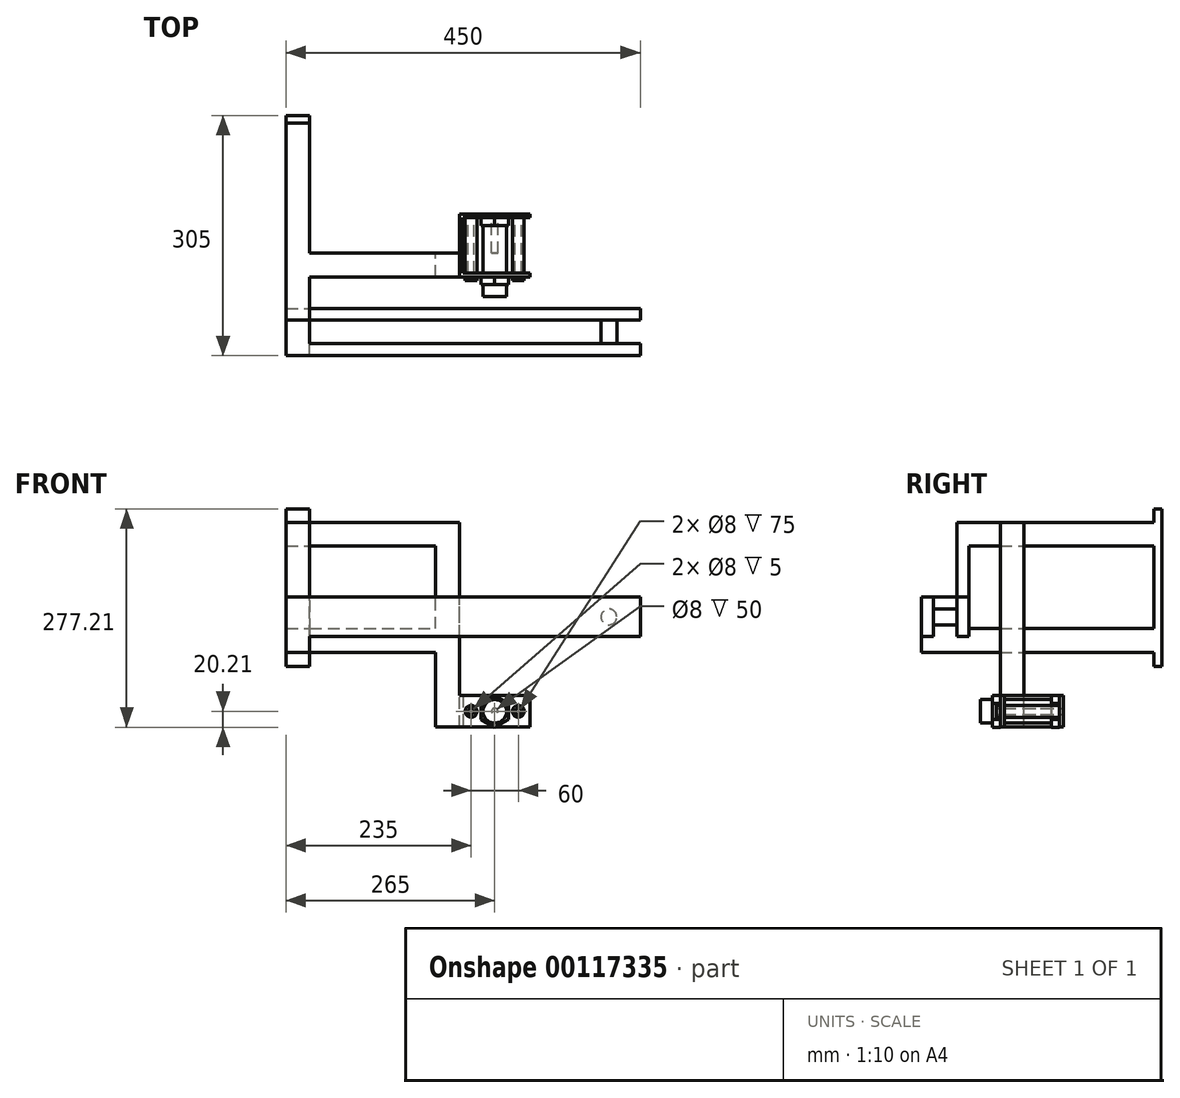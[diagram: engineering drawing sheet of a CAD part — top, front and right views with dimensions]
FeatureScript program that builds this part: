
annotation { "Feature Type Name" : "Feature", "Feature Type Description" : "" }
export const myFeature = defineFeature(function(context is Context, id is Id, definition is map)
    precondition{}
    {
        {
            var Q0;
            Q0=qCreatedBy(makeId("Front.planeOp"),FACE);
            var sketch = newSketch(context, id + "F0", { "sketchPlane" : qUnion([Q0])});
            skLineSegment(sketch, "E0.bottom", {"start": v(45, -20) * mm, "end": v(-45, -20) * mm});
            skLineSegment(sketch, "E0.top", {"start": v(45, 20) * mm, "end": v(-45, 20) * mm});
            skLineSegment(sketch, "E0.left", {"start": v(45, -20) * mm, "end": v(45, 20) * mm});
            skLineSegment(sketch, "E0.right", {"start": v(-45, -20) * mm, "end": v(-45, 20) * mm});
            skPoint(sketch, "E0.middle", {"position": v(0, 0) * mm});
            skCircle(sketch, "E1", {"center": v(0, 0) * mm, "radius": 4 * mm});
            skCircle(sketch, "E2", {"center": v(30, 0) * mm, "radius": 4 * mm});
            skCircle(sketch, "E3", {"center": v(-30, 0) * mm, "radius": 4 * mm});
            skSolve(sketch);
        }
        {
            var Q0;
            Q0 = qSketchRegion(id + "F0", true);
            extrude(context, id + "F1", {"entities" : qUnion([Q0]), "depth" : 5 * mm});
        }
        {
            var Q0;
            Q0=makeQuery(id+"F1.opExtrude","CAP_FACE",FACE,{"disambiguationData":[OSD([sQuery(id+"F0.wireOp",EDGE,"E0.bottom"),sQuery(id+"F0.wireOp",EDGE,"E0.top"),sQuery(id+"F0.wireOp",EDGE,"E0.left"),sQuery(id+"F0.wireOp",EDGE,"E0.right"),sQuery(id+"F0.wireOp",EDGE,"E1"),sQuery(id+"F0.wireOp",EDGE,"E2"),sQuery(id+"F0.wireOp",EDGE,"E3")])],"isStart":false});
            var sketch = newSketch(context, id + "F2", { "sketchPlane" : qUnion([Q0])});
            skCircle(sketch, "E4.cCircle", {"center": v(0, 0) * mm, "radius": 17.5 * mm, "construction": true});
            skLineSegment(sketch, "E4.0", {"start": v(17.5, 10.1) * mm, "end": v(17.5, -10.1) * mm});
            skLineSegment(sketch, "E4.1", {"start": v(17.5, -10.1) * mm, "end": v(0, -20.2) * mm});
            skLineSegment(sketch, "E4.2", {"start": v(0, -20.2) * mm, "end": v(-17.5, -10.1) * mm});
            skLineSegment(sketch, "E4.3", {"start": v(-17.5, -10.1) * mm, "end": v(-17.5, 10.1) * mm});
            skLineSegment(sketch, "E4.4", {"start": v(-17.5, 10.1) * mm, "end": v(0, 20.2) * mm});
            skLineSegment(sketch, "E4.5", {"start": v(0, 20.2) * mm, "end": v(17.5, 10.1) * mm});
            skPoint(sketch, "E4.0.midPoint", {"position": v(17.5, 0) * mm});
            skSolve(sketch);
        }
        {
            var Q0;
            Q0 = qSketchRegion(id + "F2", true);
            extrude(context, id + "F3", {"entities" : qUnion([Q0]), "operationType" : NewBodyOperationType.ADD, "depth" : 10 * mm});
        }
        {
            var Q0;
            Q0=makeQuery(id+"F3.opExtrude","CAP_FACE",FACE,{"disambiguationData":[OSD([sQuery(id+"F2.wireOp",EDGE,"E4.0"),sQuery(id+"F2.wireOp",EDGE,"E4.1"),sQuery(id+"F2.wireOp",EDGE,"E4.2"),sQuery(id+"F2.wireOp",EDGE,"E4.3"),sQuery(id+"F2.wireOp",EDGE,"E4.4"),sQuery(id+"F2.wireOp",EDGE,"E4.5")])],"isStart":false});
            var sketch = newSketch(context, id + "F4", { "sketchPlane" : qUnion([Q0])});
            skCircle(sketch, "E5", {"center": v(0, 0) * mm, "radius": 15 * mm});
            skSolve(sketch);
        }
        {
            var Q0;
            Q0 = qSketchRegion(id + "F4", true);
            extrude(context, id + "F5", {"entities" : qUnion([Q0]), "operationType" : NewBodyOperationType.ADD, "depth" : 60 * mm});
        }
        {
            var Q0;
            {var subQ0=sQuery(id+"F0.wireOp",EDGE,"E2");var subQ2=sQuery(id+"F0.wireOp",EDGE,"E0.left");var subQ5=sQuery(id+"F0.wireOp",EDGE,"E0.top");var subQ6=sQuery(id+"F0.wireOp",EDGE,"E0.bottom");Q0=makeQuery(id+"F3.boolean.opBoolean","SPLIT",FACE,{"disambiguationData":[TD([makeQuery(id+"F1.opExtrude","SWEPT_FACE",FACE,{"disambiguationData":[OSD([subQ2])]})])],"derivedFrom":makeQuery(id+"F1.opExtrude","CAP_FACE",FACE,{"disambiguationData":[OSD([subQ6,subQ5,subQ2,sQuery(id+"F0.wireOp",EDGE,"E0.right"),sQuery(id+"F0.wireOp",EDGE,"E1"),subQ0,sQuery(id+"F0.wireOp",EDGE,"E3")])],"isStart":false})});}
            var sketch = newSketch(context, id + "F6", { "sketchPlane" : qUnion([Q0])});
            skCircle(sketch, "E6", {"center": v(30, 0) * mm, "radius": 7.5 * mm});
            skCircle(sketch, "E7", {"center": v(-30, 0) * mm, "radius": 7.5 * mm});
            skCircle(sketch, "E8", {"center": v(30, 0) * mm, "radius": 4 * mm});
            skCircle(sketch, "E9", {"center": v(-30, 0) * mm, "radius": 4 * mm});
            skSolve(sketch);
        }
        {
            var Q0;
            Q0 = qSketchRegion(id + "F6", true);
            extrude(context, id + "F7", {"entities" : qUnion([Q0]), "operationType" : NewBodyOperationType.ADD, "depth" : 80 * mm});
        }
        {
            var Q0;
            Q0=makeQuery(id+"F5.opExtrude","CAP_FACE",FACE,{"disambiguationData":[OSD([sQuery(id+"F4.wireOp",EDGE,"E5")])],"isStart":false});
            var sketch = newSketch(context, id + "F8", { "sketchPlane" : qUnion([Q0])});
            skLineSegment(sketch, "E10.bottom", {"start": v(45, -20) * mm, "end": v(-45, -20) * mm});
            skLineSegment(sketch, "E10.top", {"start": v(45, 20) * mm, "end": v(-45, 20) * mm});
            skLineSegment(sketch, "E10.left", {"start": v(45, -20) * mm, "end": v(45, 20) * mm});
            skLineSegment(sketch, "E10.right", {"start": v(-45, -20) * mm, "end": v(-45, 20) * mm});
            skPoint(sketch, "E10.middle", {"position": v(0, 0) * mm});
            skSolve(sketch);
        }
        {
            var Q0;
            Q0 = qSketchRegion(id + "F8", true);
            extrude(context, id + "F9", {"entities" : qUnion([Q0]), "operationType" : NewBodyOperationType.ADD, "depth" : 5 * mm});
        }
        {
            var Q0;
            Q0=makeQuery(id+"F9.opExtrude","CAP_FACE",FACE,{"disambiguationData":[OSD([sQuery(id+"F8.wireOp",EDGE,"E10.bottom"),sQuery(id+"F8.wireOp",EDGE,"E10.top"),sQuery(id+"F8.wireOp",EDGE,"E10.left"),sQuery(id+"F8.wireOp",EDGE,"E10.right")])],"isStart":false});
            var sketch = newSketch(context, id + "F10", { "sketchPlane" : qUnion([Q0])});
            skCircle(sketch, "E11.cCircle", {"center": v(0, 0) * mm, "radius": 17.5 * mm, "construction": true});
            skLineSegment(sketch, "E11.0", {"start": v(17.52, -10.07) * mm, "end": v(0.04, -20.2) * mm});
            skLineSegment(sketch, "E11.1", {"start": v(0.04, -20.2) * mm, "end": v(-17.48, -10.14) * mm});
            skLineSegment(sketch, "E11.2", {"start": v(-17.48, -10.14) * mm, "end": v(-17.52, 10.07) * mm});
            skLineSegment(sketch, "E11.3", {"start": v(-17.52, 10.07) * mm, "end": v(-0.04, 20.2) * mm});
            skLineSegment(sketch, "E11.4", {"start": v(-0.04, 20.2) * mm, "end": v(17.48, 10.14) * mm});
            skLineSegment(sketch, "E11.5", {"start": v(17.48, 10.14) * mm, "end": v(17.52, -10.07) * mm});
            skPoint(sketch, "E11.0.midPoint", {"position": v(8.78, -15.14) * mm});
            skSolve(sketch);
        }
        {
            var Q0;
            Q0 = qSketchRegion(id + "F10", true);
            extrude(context, id + "F11", {"entities" : qUnion([Q0]), "operationType" : NewBodyOperationType.ADD, "depth" : 10 * mm});
        }
        {
            var Q0;
            Q0=makeQuery(id+"F11.opExtrude","CAP_FACE",FACE,{"disambiguationData":[OSD([sQuery(id+"F10.wireOp",EDGE,"E11.0"),sQuery(id+"F10.wireOp",EDGE,"E11.1"),sQuery(id+"F10.wireOp",EDGE,"E11.2"),sQuery(id+"F10.wireOp",EDGE,"E11.3"),sQuery(id+"F10.wireOp",EDGE,"E11.4"),sQuery(id+"F10.wireOp",EDGE,"E11.5")])],"isStart":false});
            var sketch = newSketch(context, id + "F12", { "sketchPlane" : qUnion([Q0])});
            skCircle(sketch, "E12", {"center": v(0, 0) * mm, "radius": 15 * mm});
            skSolve(sketch);
        }
        {
            var Q0;
            Q0 = qSketchRegion(id + "F12", true);
            extrude(context, id + "F13", {"entities" : qUnion([Q0]), "operationType" : NewBodyOperationType.ADD, "depth" : 15 * mm});
        }
        {
            var Q0;
            {var subQ0=sQuery(id+"F0.wireOp",EDGE,"E0.right");var subQ1=sQuery(id+"F0.wireOp",EDGE,"E3");var subQ3=sQuery(id+"F0.wireOp",EDGE,"E0.top");var subQ4=sQuery(id+"F0.wireOp",EDGE,"E0.bottom");Q0=makeQuery(id+"F3.boolean.opBoolean","SPLIT",FACE,{"disambiguationData":[TD([makeQuery(id+"F1.opExtrude","SWEPT_FACE",FACE,{"disambiguationData":[OSD([subQ0])]})])],"derivedFrom":makeQuery(id+"F1.opExtrude","CAP_FACE",FACE,{"disambiguationData":[OSD([subQ4,subQ3,sQuery(id+"F0.wireOp",EDGE,"E0.left"),subQ0,sQuery(id+"F0.wireOp",EDGE,"E1"),sQuery(id+"F0.wireOp",EDGE,"E2"),subQ1])],"isStart":false})});}
            var sketch = newSketch(context, id + "F14", { "sketchPlane" : qUnion([Q0])});
            skLineSegment(sketch, "E13.bottom", {"start": v(-45, 20) * mm, "end": v(-40, 20) * mm});
            skLineSegment(sketch, "E13.top", {"start": v(-45, -20) * mm, "end": v(-40, -20) * mm});
            skLineSegment(sketch, "E13.left", {"start": v(-45, 20) * mm, "end": v(-45, -20) * mm});
            skLineSegment(sketch, "E13.right", {"start": v(-40, 20) * mm, "end": v(-40, -20) * mm});
            skSolve(sketch);
        }
        {
            var Q0;
            Q0 = qSketchRegion(id + "F14", true);
            var Q1;
            {var subQ0=sQuery(id+"F8.wireOp",EDGE,"E10.bottom");var subQ1=sQuery(id+"F8.wireOp",EDGE,"E10.right");var subQ2=sQuery(id+"F8.wireOp",EDGE,"E10.top");var subQ3=sQuery(id+"F8.wireOp",EDGE,"E10.left");Q1=makeQuery(id+"F9.boolean.opBoolean","SPLIT",FACE,{"disambiguationData":[TD([makeQuery(id+"F5.opExtrude","SWEPT_FACE",FACE,{"disambiguationData":[OSD([sQuery(id+"F4.wireOp",EDGE,"E5")])]})])],"derivedFrom":makeQuery(id+"F9.opExtrude","CAP_FACE",FACE,{"disambiguationData":[OSD([subQ0,subQ2,subQ3,subQ1])],"isStart":true})});}
            extrude(context, id + "F15", {"entities" : qUnion([Q0]), "operationType" : NewBodyOperationType.ADD, "endBound" : BoundingType.UP_TO_SURFACE, "endBoundEntityFace" : qUnion([Q1]), "depth" : 25 * mm});
        }
        {
            var Q0;
            Q0=makeQuery(id+"F1.opExtrude","CAP_FACE",FACE,{"disambiguationData":[OSD([sQuery(id+"F0.wireOp",EDGE,"E0.bottom"),sQuery(id+"F0.wireOp",EDGE,"E0.top"),sQuery(id+"F0.wireOp",EDGE,"E0.left"),sQuery(id+"F0.wireOp",EDGE,"E0.right"),sQuery(id+"F0.wireOp",EDGE,"E1"),sQuery(id+"F0.wireOp",EDGE,"E2"),sQuery(id+"F0.wireOp",EDGE,"E3")])],"isStart":true});
            var sketch = newSketch(context, id + "F16", { "sketchPlane" : qUnion([Q0])});
            skCircle(sketch, "E14", {"center": v(0, 0) * mm, "radius": 4 * mm});
            skSolve(sketch);
        }
        {
            var Q0;
            Q0 = qSketchRegion(id + "F16", true);
            extrude(context, id + "F17", {"entities" : qUnion([Q0]), "operationType" : NewBodyOperationType.REMOVE, "oppositeDirection" : true, "depth" : 50 * mm});
        }
        {
            var Q0;
            Q0=makeQuery(id+"F15.boolean.opBoolean","MERGE",FACE,{"derivedFrom":[makeQuery(id+"F1.opExtrude","SWEPT_FACE",FACE,{"disambiguationData":[OSD([sQuery(id+"F0.wireOp",EDGE,"E0.right")])]}),makeQuery(id+"F9.opExtrude","SWEPT_FACE",FACE,{"disambiguationData":[OSD([sQuery(id+"F8.wireOp",EDGE,"E10.right")])]}),makeQuery(id+"F15.opExtrude","SWEPT_FACE",FACE,{"disambiguationData":[OSD([sQuery(id+"F14.wireOp",EDGE,"E13.left")])]})]});
            var sketch = newSketch(context, id + "F18", { "sketchPlane" : qUnion([Q0])});
            skLineSegment(sketch, "E15.bottom", {"start": v(80, -20) * mm, "end": v(50, -20) * mm});
            skLineSegment(sketch, "E15.top", {"start": v(80, 240) * mm, "end": v(50, 240) * mm});
            skLineSegment(sketch, "E15.left", {"start": v(80, -20) * mm, "end": v(80, 240) * mm});
            skLineSegment(sketch, "E15.right", {"start": v(50, -20) * mm, "end": v(50, 240) * mm});
            skSolve(sketch);
        }
        {
            var Q0;
            Q0 = qSketchRegion(id + "F18", true);
            extrude(context, id + "F19", {"entities" : qUnion([Q0]), "operationType" : NewBodyOperationType.ADD, "depth" : 30 * mm});
        }
        {
            var Q0;
            Q0=makeQuery(id+"F19.opExtrude","CAP_FACE",FACE,{"disambiguationData":[OSD([sQuery(id+"F18.wireOp",EDGE,"E15.bottom"),sQuery(id+"F18.wireOp",EDGE,"E15.top"),sQuery(id+"F18.wireOp",EDGE,"E15.left"),sQuery(id+"F18.wireOp",EDGE,"E15.right")])],"isStart":false});
            var sketch = newSketch(context, id + "F20", { "sketchPlane" : qUnion([Q0])});
            skLineSegment(sketch, "E16.bottom", {"start": v(80, 75) * mm, "end": v(50, 75) * mm});
            skLineSegment(sketch, "E16.top", {"start": v(80, 105) * mm, "end": v(50, 105) * mm});
            skLineSegment(sketch, "E16.left", {"start": v(80, 75) * mm, "end": v(80, 105) * mm});
            skLineSegment(sketch, "E16.right", {"start": v(50, 75) * mm, "end": v(50, 105) * mm});
            skLineSegment(sketch, "E17.bottom", {"start": v(80, 240) * mm, "end": v(50, 240) * mm});
            skLineSegment(sketch, "E17.top", {"start": v(80, 210) * mm, "end": v(50, 210) * mm});
            skLineSegment(sketch, "E17.left", {"start": v(80, 240) * mm, "end": v(80, 210) * mm});
            skLineSegment(sketch, "E17.right", {"start": v(50, 240) * mm, "end": v(50, 210) * mm});
            skSolve(sketch);
        }
        {
            var Q0;
            Q0 = qSketchRegion(id + "F20", true);
            extrude(context, id + "F21", {"entities" : qUnion([Q0]), "operationType" : NewBodyOperationType.ADD, "depth" : 190 * mm});
        }
        {
            var Q0;
            {var subQ0=sQuery(id+"F8.wireOp",EDGE,"E10.right");var subQ2=sQuery(id+"F8.wireOp",EDGE,"E10.top");var subQ4=sQuery(id+"F8.wireOp",EDGE,"E10.bottom");var subQ6=makeQuery(id+"F7.opExtrude","SWEPT_FACE",FACE,{"disambiguationData":[OSD([sQuery(id+"F6.wireOp",EDGE,"E7")])]});var subQ10=sQuery(id+"F8.wireOp",EDGE,"E10.left");Q0=makeQuery(id+"F21.boolean.opBoolean","MERGE",FACE,{"derivedFrom":[makeQuery(id+"F19.boolean.opBoolean","MERGE",FACE,{"derivedFrom":[makeQuery(id+"F11.boolean.opBoolean","SPLIT",FACE,{"disambiguationData":[TD([subQ6])],"derivedFrom":makeQuery(id+"F9.boolean.opBoolean","SPLIT",FACE,{"disambiguationData":[TD([makeQuery(id+"F7.opExtrude","SWEPT_FACE",FACE,{"disambiguationData":[OSD([sQuery(id+"F6.wireOp",EDGE,"E6")])]})])],"derivedFrom":makeQuery(id+"F9.opExtrude","CAP_FACE",FACE,{"disambiguationData":[OSD([subQ4,subQ2,subQ10,subQ0])],"isStart":false})})}),makeQuery(id+"F19.opExtrude","SWEPT_FACE",FACE,{"disambiguationData":[OSD([sQuery(id+"F18.wireOp",EDGE,"E15.left")])]})]}),makeQuery(id+"F21.opExtrude","SWEPT_FACE",FACE,{"disambiguationData":[OSD([sQuery(id+"F20.wireOp",EDGE,"E16.left")])]}),makeQuery(id+"F21.opExtrude","SWEPT_FACE",FACE,{"disambiguationData":[OSD([sQuery(id+"F20.wireOp",EDGE,"E17.left")])]})]});}
            var sketch = newSketch(context, id + "F22", { "sketchPlane" : qUnion([Q0])});
            skLineSegment(sketch, "E18.bottom", {"start": v(-265, 75) * mm, "end": v(-235, 75) * mm});
            skLineSegment(sketch, "E18.top", {"start": v(-265, 105) * mm, "end": v(-235, 105) * mm});
            skLineSegment(sketch, "E18.left", {"start": v(-265, 75) * mm, "end": v(-265, 105) * mm});
            skLineSegment(sketch, "E18.right", {"start": v(-235, 75) * mm, "end": v(-235, 105) * mm});
            skLineSegment(sketch, "E19.bottom", {"start": v(-265, 210) * mm, "end": v(-235, 210) * mm});
            skLineSegment(sketch, "E19.top", {"start": v(-265, 240) * mm, "end": v(-235, 240) * mm});
            skLineSegment(sketch, "E19.left", {"start": v(-265, 210) * mm, "end": v(-265, 240) * mm});
            skLineSegment(sketch, "E19.right", {"start": v(-235, 210) * mm, "end": v(-235, 240) * mm});
            skSolve(sketch);
        }
        {
            var Q0;
            Q0 = qSketchRegion(id + "F22", true);
            extrude(context, id + "F23", {"entities" : qUnion([Q0]), "operationType" : NewBodyOperationType.ADD, "oppositeDirection" : true, "depth" : 205 * mm});
        }
        {
            var Q0;
            Q0 = qSketchRegion(id + "F22", true);
            extrude(context, id + "F24", {"entities" : qUnion([Q0]), "operationType" : NewBodyOperationType.ADD, "depth" : 40 * mm});
        }
        {
            var Q0;
            Q0=makeQuery(id+"F23.opExtrude","CAP_FACE",FACE,{"disambiguationData":[OSD([sQuery(id+"F22.wireOp",EDGE,"E18.bottom"),sQuery(id+"F22.wireOp",EDGE,"E18.top"),sQuery(id+"F22.wireOp",EDGE,"E18.left"),sQuery(id+"F22.wireOp",EDGE,"E18.right")])],"isStart":false});
            var sketch = newSketch(context, id + "F25", { "sketchPlane" : qUnion([Q0])});
            skLineSegment(sketch, "E20.bottom", {"start": v(265, 257) * mm, "end": v(235, 257) * mm});
            skLineSegment(sketch, "E20.top", {"start": v(265, 57) * mm, "end": v(235, 57) * mm});
            skLineSegment(sketch, "E20.left", {"start": v(265, 257) * mm, "end": v(265, 57) * mm});
            skLineSegment(sketch, "E20.right", {"start": v(235, 257) * mm, "end": v(235, 57) * mm});
            skSolve(sketch);
        }
        {
            var Q0;
            Q0 = qSketchRegion(id + "F25", true);
            extrude(context, id + "F26", {"entities" : qUnion([Q0]), "operationType" : NewBodyOperationType.ADD, "oppositeDirection" : true, "depth" : 10 * mm});
        }
        {
            var Q0;
            Q0=makeQuery(id+"F24.opExtrude","CAP_FACE",FACE,{"disambiguationData":[OSD([sQuery(id+"F22.wireOp",EDGE,"E18.bottom"),sQuery(id+"F22.wireOp",EDGE,"E18.top"),sQuery(id+"F22.wireOp",EDGE,"E18.left"),sQuery(id+"F22.wireOp",EDGE,"E18.right")])],"isStart":false});
            var sketch = newSketch(context, id + "F27", { "sketchPlane" : qUnion([Q0])});
            skLineSegment(sketch, "E21.bottom", {"start": v(-265, 75) * mm, "end": v(-235, 75) * mm});
            skLineSegment(sketch, "E21.top", {"start": v(-265, 240) * mm, "end": v(-235, 240) * mm});
            skLineSegment(sketch, "E21.left", {"start": v(-265, 75) * mm, "end": v(-265, 240) * mm});
            skLineSegment(sketch, "E21.right", {"start": v(-235, 75) * mm, "end": v(-235, 240) * mm});
            skSolve(sketch);
        }
        {
            var Q0;
            Q0 = qSketchRegion(id + "F27", true);
            extrude(context, id + "F28", {"entities" : qUnion([Q0]), "operationType" : NewBodyOperationType.ADD, "depth" : 60 * mm});
        }
        {
            var Q0;
            Q0=makeQuery(id+"F28.boolean.opBoolean","MERGE",FACE,{"derivedFrom":[makeQuery(id+"F24.opExtrude","SWEPT_FACE",FACE,{"disambiguationData":[OSD([sQuery(id+"F22.wireOp",EDGE,"E18.right")])]}),makeQuery(id+"F24.opExtrude","SWEPT_FACE",FACE,{"disambiguationData":[OSD([sQuery(id+"F22.wireOp",EDGE,"E19.right")])]}),makeQuery(id+"F28.opExtrude","SWEPT_FACE",FACE,{"disambiguationData":[OSD([sQuery(id+"F27.wireOp",EDGE,"E21.right")])]})]});
            var sketch = newSketch(context, id + "F29", { "sketchPlane" : qUnion([Q0])});
            skLineSegment(sketch, "E22.bottom", {"start": v(-180, 95) * mm, "end": v(-165, 95) * mm});
            skLineSegment(sketch, "E22.top", {"start": v(-180, 145) * mm, "end": v(-165, 145) * mm});
            skLineSegment(sketch, "E22.left", {"start": v(-180, 95) * mm, "end": v(-180, 145) * mm});
            skLineSegment(sketch, "E22.right", {"start": v(-120, 95) * mm, "end": v(-120, 145) * mm});
            skLineSegment(sketch, "E23", {"start": v(-165, 95) * mm, "end": v(-165, 145) * mm});
            skLineSegment(sketch, "E24", {"start": v(-135, 95) * mm, "end": v(-135, 145) * mm});
            skLineSegment(sketch, "E25.trimOffspring", {"start": v(-135, 145) * mm, "end": v(-120, 145) * mm});
            skLineSegment(sketch, "E26.trimOffspring", {"start": v(-135, 95) * mm, "end": v(-120, 95) * mm});
            skSolve(sketch);
        }
        {
            var Q0;
            Q0 = qSketchRegion(id + "F29", true);
            extrude(context, id + "F30", {"entities" : qUnion([Q0]), "operationType" : NewBodyOperationType.ADD, "depth" : 420 * mm});
        }
        {
            var Q0;
            Q0=makeQuery(id+"F28.boolean.opBoolean","MERGE",FACE,{"derivedFrom":[makeQuery(id+"F24.opExtrude","SWEPT_FACE",FACE,{"disambiguationData":[OSD([sQuery(id+"F22.wireOp",EDGE,"E18.right")])]}),makeQuery(id+"F24.opExtrude","SWEPT_FACE",FACE,{"disambiguationData":[OSD([sQuery(id+"F22.wireOp",EDGE,"E19.right")])]}),makeQuery(id+"F28.opExtrude","SWEPT_FACE",FACE,{"disambiguationData":[OSD([sQuery(id+"F27.wireOp",EDGE,"E21.right")])]})]});
            var sketch = newSketch(context, id + "F31", { "sketchPlane" : qUnion([Q0])});
            skLineSegment(sketch, "E27.bottom", {"start": v(-180, 145) * mm, "end": v(-135, 145) * mm});
            skLineSegment(sketch, "E27.top", {"start": v(-180, 266.34) * mm, "end": v(-135, 266.34) * mm});
            skLineSegment(sketch, "E27.left", {"start": v(-180, 145) * mm, "end": v(-180, 266.34) * mm});
            skLineSegment(sketch, "E27.right", {"start": v(-135, 145) * mm, "end": v(-135, 266.34) * mm});
            skSolve(sketch);
        }
        {
            var Q0;
            Q0 = qSketchRegion(id + "F31", true);
            extrude(context, id + "F32", {"entities" : qUnion([Q0]), "operationType" : NewBodyOperationType.REMOVE, "oppositeDirection" : true, "depth" : 40 * mm});
        }
        {
            var Q0;
            Q0=makeQuery(id+"F30.boolean.opBoolean","MERGE",FACE,{"derivedFrom":[makeQuery(id+"F28.opExtrude","CAP_FACE",FACE,{"disambiguationData":[OSD([sQuery(id+"F27.wireOp",EDGE,"E21.bottom"),sQuery(id+"F27.wireOp",EDGE,"E21.top"),sQuery(id+"F27.wireOp",EDGE,"E21.left"),sQuery(id+"F27.wireOp",EDGE,"E21.right")])],"isStart":false}),makeQuery(id+"F30.opExtrude","SWEPT_FACE",FACE,{"disambiguationData":[OSD([sQuery(id+"F29.wireOp",EDGE,"E22.left")])]})]});
            var sketch = newSketch(context, id + "F33", { "sketchPlane" : qUnion([Q0])});
            skCircle(sketch, "E28", {"center": v(145, 120) * mm, "radius": 10 * mm});
            skPoint(sketch, "E28.centerSnap0", {"position": v(185, 120) * mm});
            skSolve(sketch);
        }
        {
            var Q0;
            Q0 = qSketchRegion(id + "F33", true);
            extrude(context, id + "F34", {"entities" : qUnion([Q0]), "operationType" : NewBodyOperationType.ADD, "oppositeDirection" : true, "depth" : 60 * mm});
        }
    });
